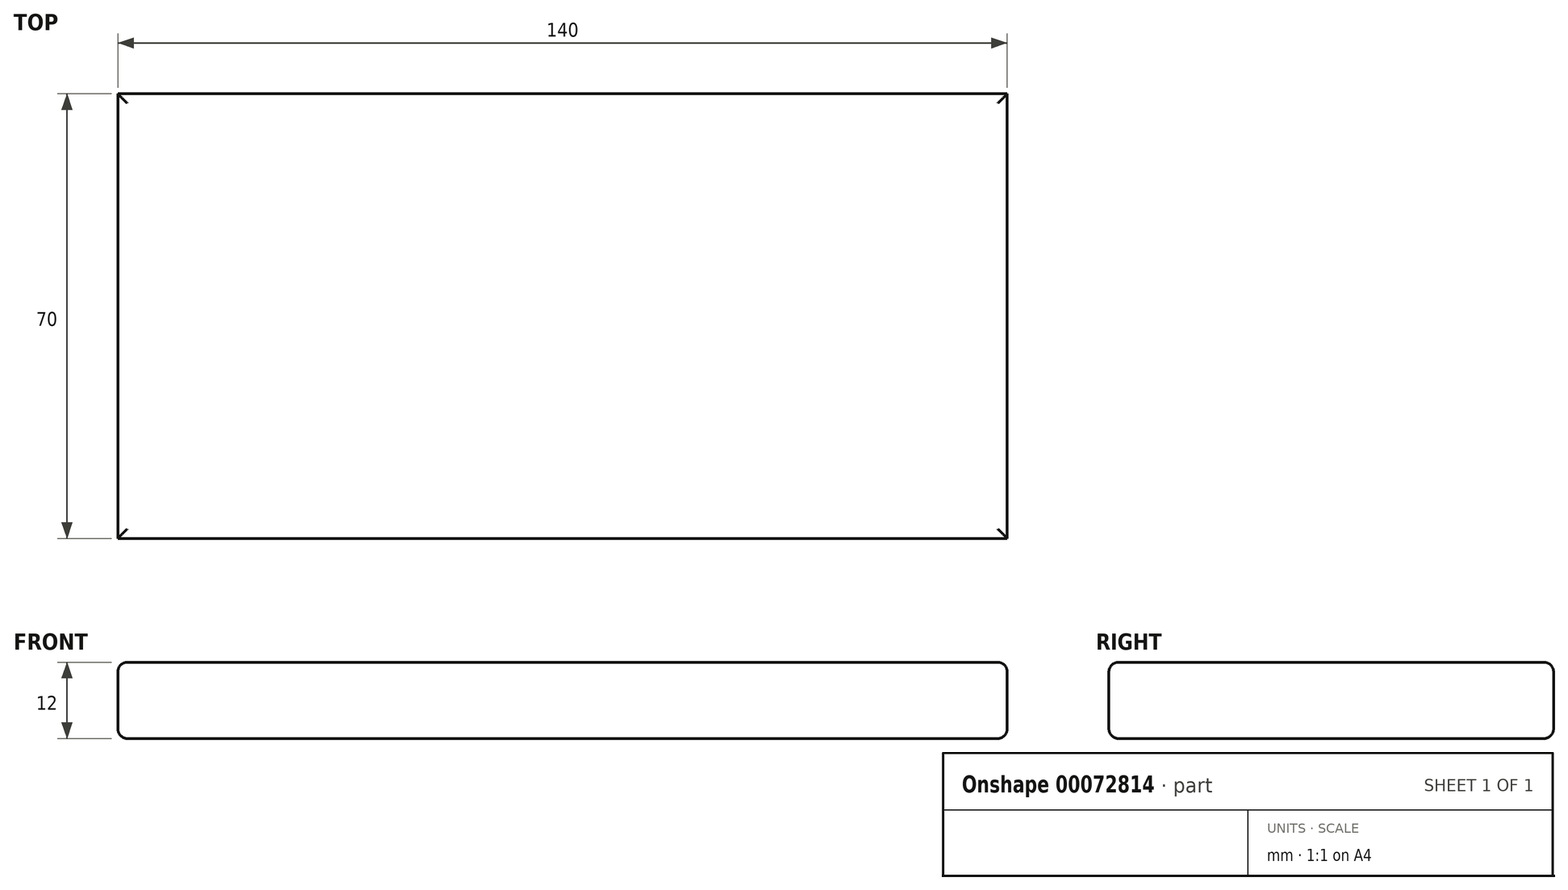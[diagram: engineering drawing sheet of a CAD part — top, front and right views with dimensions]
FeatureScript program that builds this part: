
annotation { "Feature Type Name" : "Feature", "Feature Type Description" : "" }
export const myFeature = defineFeature(function(context is Context, id is Id, definition is map)
    precondition{}
    {
        {
            var Q0;
            Q0=qCreatedBy(makeId("Top.planeOp"),FACE);
            var sketch = newSketch(context, id + "F0", { "sketchPlane" : qUnion([Q0])});
            skLineSegment(sketch, "E0.bottom", {"start": v(0, 0) * mm, "end": v(140, 0) * mm});
            skLineSegment(sketch, "E0.top", {"start": v(0, 70) * mm, "end": v(140, 70) * mm});
            skLineSegment(sketch, "E0.left", {"start": v(0, 0) * mm, "end": v(0, 70) * mm});
            skLineSegment(sketch, "E0.right", {"start": v(140, 0) * mm, "end": v(140, 70) * mm});
            skSolve(sketch);
        }
        {
            var Q0;
            Q0=makeQuery(id+"F0.imprint","IMPRINT",FACE,{"disambiguationData":[TD([[makeQuery(id+"F0.imprint","IMPRINT",EDGE,{"derivedFrom":sQuery(id+"F0.wireOp",EDGE,"E0.bottom")}),1.0]])]});
            extrude(context, id + "F1", {"entities" : qUnion([Q0]), "depth" : 12 * mm});
        }
        {
            var Q0;
            Q0=makeQuery(id+"F1.opExtrude","CAP_FACE",FACE,{"disambiguationData":[OSD([sQuery(id+"F0.wireOp",EDGE,"E0.bottom"),sQuery(id+"F0.wireOp",EDGE,"E0.top"),sQuery(id+"F0.wireOp",EDGE,"E0.left"),sQuery(id+"F0.wireOp",EDGE,"E0.right")])],"isStart":false});
            var Q1;
            Q1=makeQuery(id+"F1.opExtrude","CAP_FACE",FACE,{"disambiguationData":[OSD([sQuery(id+"F0.wireOp",EDGE,"E0.bottom"),sQuery(id+"F0.wireOp",EDGE,"E0.top"),sQuery(id+"F0.wireOp",EDGE,"E0.left"),sQuery(id+"F0.wireOp",EDGE,"E0.right")])],"isStart":true});
            fillet(context, id + "F2", {"entities" : qUnion([Q0, Q1]), "radius" : 1.5 * mm, "tangentPropagation" : true, "allowEdgeOverflow" : false});
        }
    });
